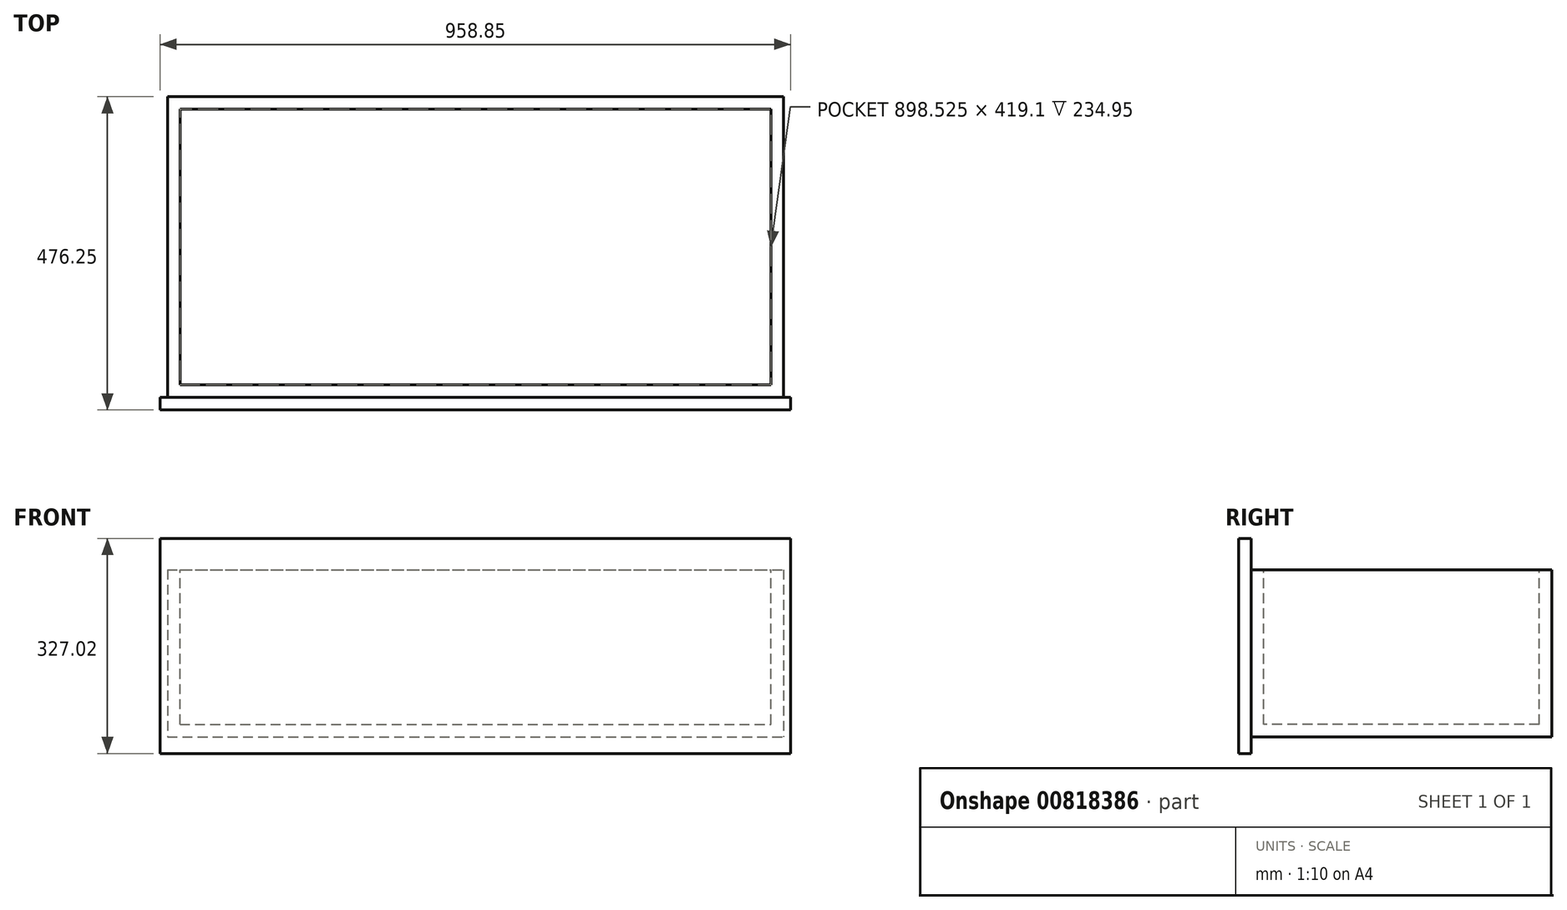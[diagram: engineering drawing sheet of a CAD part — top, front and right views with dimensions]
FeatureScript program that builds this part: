
annotation { "Feature Type Name" : "Feature", "Feature Type Description" : "" }
export const myFeature = defineFeature(function(context is Context, id is Id, definition is map)
    precondition{}
    {
        {
            var Q0;
            Q0=qCreatedBy(makeId("Top.planeOp"),FACE);
            var sketch = newSketch(context, id + "F0", { "sketchPlane" : qUnion([Q0])});
            skLineSegment(sketch, "E0.bottom", {"start": v(-480.42, 234.5) * mm, "end": v(456.2, 234.5) * mm});
            skLineSegment(sketch, "E0.top", {"start": v(-480.42, -222.7) * mm, "end": v(456.2, -222.7) * mm});
            skLineSegment(sketch, "E0.left", {"start": v(-480.42, 234.5) * mm, "end": v(-480.42, -222.7) * mm});
            skLineSegment(sketch, "E0.right", {"start": v(456.2, 234.5) * mm, "end": v(456.2, -222.7) * mm});
            skLineSegment(sketch, "E1", {"start": v(-480.42, 234.5) * mm, "end": v(456.2, -222.7) * mm, "construction": true});
            skSolve(sketch);
        }
        {
            var Q0;
            Q0 = qSketchRegion(id + "F0", true);
            extrude(context, id + "F1", {"entities" : qUnion([Q0]), "depth" : 254 * mm, "offsetDistance" : 25.4 * mm});
        }
        {
            var Q0;
            Q0=makeQuery(id+"F1.opExtrude","CAP_FACE",FACE,{"disambiguationData":[OSD([sQuery(id+"F0.wireOp",EDGE,"E0.bottom"),sQuery(id+"F0.wireOp",EDGE,"E0.top"),sQuery(id+"F0.wireOp",EDGE,"E0.left"),sQuery(id+"F0.wireOp",EDGE,"E0.right")])],"isStart":false});
            var sketch = newSketch(context, id + "F2", { "sketchPlane" : qUnion([Q0])});
            skLineSegment(sketch, "E2.bottom", {"start": v(-461.37, 215.46) * mm, "end": v(437.16, 215.46) * mm});
            skLineSegment(sketch, "E2.top", {"start": v(-461.37, -203.64) * mm, "end": v(437.16, -203.64) * mm});
            skLineSegment(sketch, "E2.left", {"start": v(-461.37, 215.46) * mm, "end": v(-461.37, -203.64) * mm});
            skLineSegment(sketch, "E2.right", {"start": v(437.16, 215.46) * mm, "end": v(437.16, -203.64) * mm});
            skSolve(sketch);
        }
        {
            var Q0;
            Q0 = qSketchRegion(id + "F2", true);
            extrude(context, id + "F3", {"entities" : qUnion([Q0]), "operationType" : NewBodyOperationType.REMOVE, "oppositeDirection" : true, "depth" : 234.95 * mm, "offsetDistance" : 25.4 * mm});
        }
        {
            var Q0;
            Q0=makeQuery(id+"F1.opExtrude","SWEPT_FACE",FACE,{"disambiguationData":[OSD([sQuery(id+"F0.wireOp",EDGE,"E0.top")])]});
            var sketch = newSketch(context, id + "F4", { "sketchPlane" : qUnion([Q0])});
            skLineSegment(sketch, "E3.bottom", {"start": v(-491.53, 301.62) * mm, "end": v(467.32, 301.63) * mm});
            skLineSegment(sketch, "E3.top", {"start": v(-491.53, -25.4) * mm, "end": v(467.32, -25.4) * mm});
            skLineSegment(sketch, "E3.left", {"start": v(-491.53, 301.62) * mm, "end": v(-491.53, -25.4) * mm});
            skLineSegment(sketch, "E3.right", {"start": v(467.32, 301.63) * mm, "end": v(467.32, -25.4) * mm});
            skSolve(sketch);
        }
        {
            var Q0;
            Q0 = qSketchRegion(id + "F4", true);
            extrude(context, id + "F5", {"entities" : qUnion([Q0]), "operationType" : NewBodyOperationType.ADD, "depth" : 19.05 * mm, "offsetDistance" : 25.4 * mm});
        }
    });
